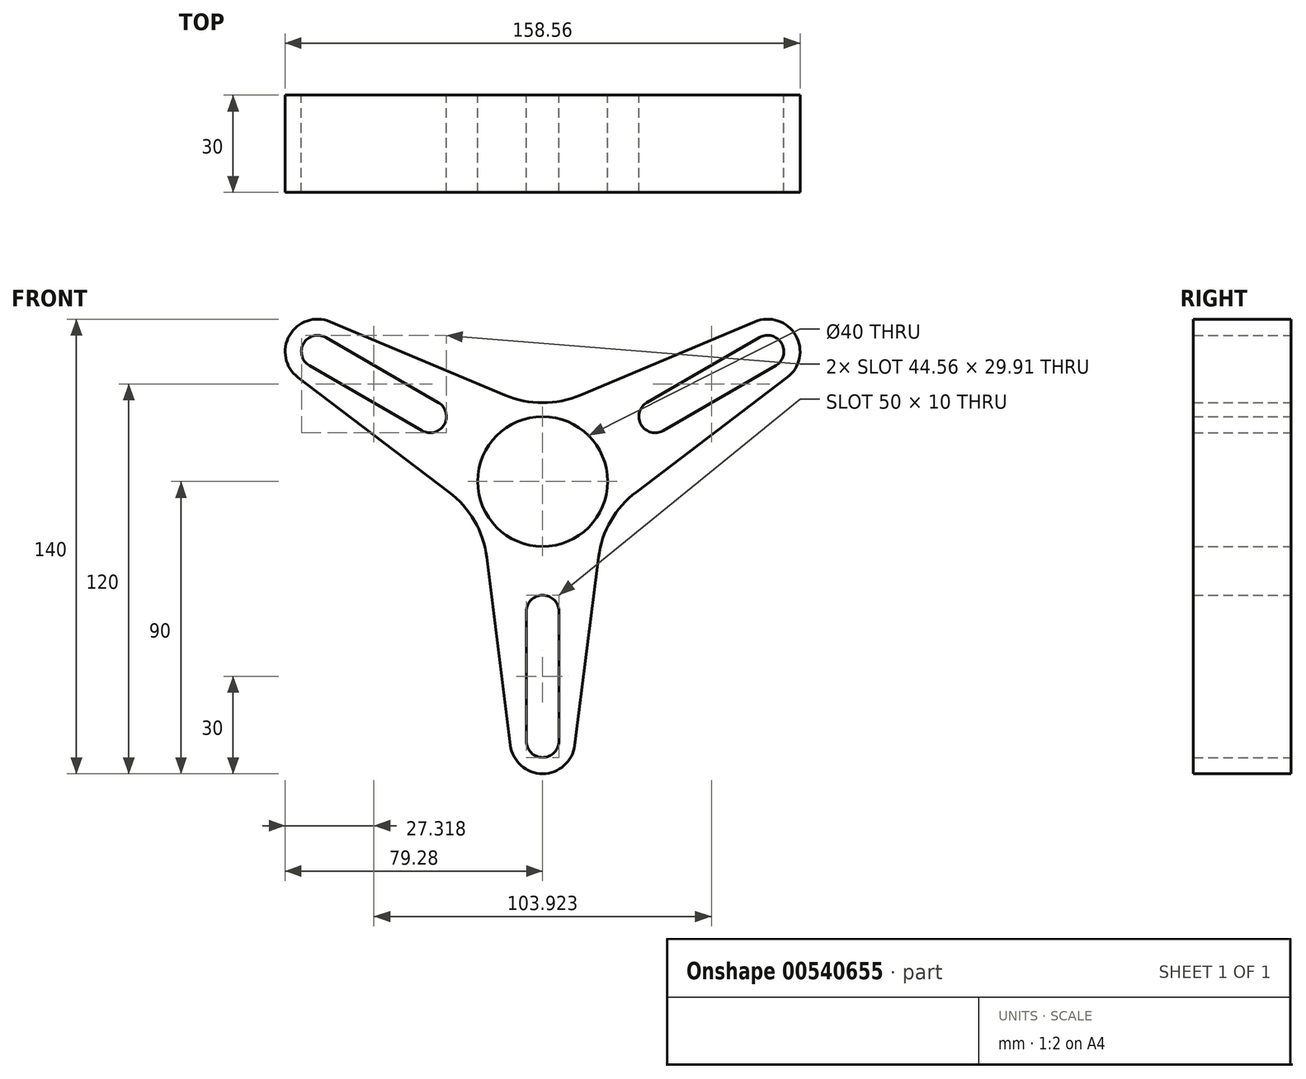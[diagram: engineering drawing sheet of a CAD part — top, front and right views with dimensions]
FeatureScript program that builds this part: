
annotation { "Feature Type Name" : "Feature", "Feature Type Description" : "" }
export const myFeature = defineFeature(function(context is Context, id is Id, definition is map)
    precondition{}
    {
        {
            var Q0;
            Q0=qCreatedBy(makeId("Front.planeOp"),FACE);
            var sketch = newSketch(context, id + "F0", { "sketchPlane" : qUnion([Q0])});
            skCircle(sketch, "E0", {"center": v(0, 0) * mm, "radius": 10 * mm});
            skCircle(sketch, "E1", {"center": v(0, 0) * mm, "radius": 20 * mm});
            skLineSegment(sketch, "E2", {"start": v(0, 0) * mm, "end": v(0, -90) * mm, "construction": true});
            skLineSegment(sketch, "E3", {"start": v(0, 0) * mm, "end": v(77.94, 45) * mm, "construction": true});
            skLineSegment(sketch, "E4", {"start": v(0, 0) * mm, "end": v(-77.94, 45) * mm, "construction": true});
            skPoint(sketch, "E5", {"position": v(0, -80) * mm});
            skPoint(sketch, "E6", {"position": v(-69.28, 40) * mm});
            skPoint(sketch, "E7", {"position": v(69.28, 40) * mm});
            skArc(sketch, "E8", {"start": v(-65.4, 49.22) * mm, "mid": v(-77.94, 45) * mm, "end": v(-75.33, 32.03) * mm});
            skArc(sketch, "E9", {"start": v(-66.78, 44.33) * mm, "mid": v(-73.61, 42.5) * mm, "end": v(-71.78, 35.67) * mm});
            skArc(sketch, "E10", {"start": v(75.33, 32.03) * mm, "mid": v(77.94, 45) * mm, "end": v(65.4, 49.22) * mm});
            skArc(sketch, "E11", {"start": v(71.78, 35.67) * mm, "mid": v(73.61, 42.5) * mm, "end": v(66.78, 44.33) * mm});
            skArc(sketch, "E12", {"start": v(-9.92, -81.25) * mm, "mid": v(0, -90) * mm, "end": v(9.92, -81.25) * mm});
            skArc(sketch, "E13", {"start": v(-5, -80) * mm, "mid": v(0, -85) * mm, "end": v(5, -80) * mm});
            skLineSegment(sketch, "E14", {"start": v(-9.92, -81.25) * mm, "end": v(-17.21, -23.37) * mm});
            skLineSegment(sketch, "E15", {"start": v(-28.85, -3.22) * mm, "end": v(-75.33, 32.03) * mm});
            skLineSegment(sketch, "E16", {"start": v(-65.4, 49.22) * mm, "end": v(-11.63, 26.6) * mm});
            skLineSegment(sketch, "E17", {"start": v(11.63, 26.6) * mm, "end": v(65.4, 49.22) * mm});
            skLineSegment(sketch, "E18", {"start": v(75.33, 32.03) * mm, "end": v(28.85, -3.22) * mm});
            skLineSegment(sketch, "E19", {"start": v(17.21, -23.37) * mm, "end": v(9.92, -81.25) * mm});
            skArc(sketch, "E20", {"start": v(-37.14, 15.67) * mm, "mid": v(-30.31, 17.5) * mm, "end": v(-32.14, 24.33) * mm});
            skArc(sketch, "E21", {"start": v(32.14, 24.33) * mm, "mid": v(30.31, 17.5) * mm, "end": v(37.14, 15.67) * mm});
            skArc(sketch, "E22", {"start": v(5, -40) * mm, "mid": v(0, -35) * mm, "end": v(-5, -40) * mm});
            skLineSegment(sketch, "E23", {"start": v(37.14, 15.67) * mm, "end": v(71.78, 35.67) * mm});
            skLineSegment(sketch, "E24", {"start": v(66.78, 44.33) * mm, "end": v(32.14, 24.33) * mm});
            skLineSegment(sketch, "E25", {"start": v(-37.14, 15.67) * mm, "end": v(-71.78, 35.67) * mm});
            skLineSegment(sketch, "E26", {"start": v(-66.78, 44.33) * mm, "end": v(-32.14, 24.33) * mm});
            skLineSegment(sketch, "E27", {"start": v(-5, -40) * mm, "end": v(-5, -80) * mm});
            skLineSegment(sketch, "E28", {"start": v(5, -40) * mm, "end": v(5, -80) * mm});
            skArc(sketch, "E29.filletArc", {"start": v(-17.21, -23.37) * mm, "mid": v(-21, -12.12) * mm, "end": v(-28.85, -3.22) * mm});
            skArc(sketch, "E30.filletArc", {"start": v(28.85, -3.22) * mm, "mid": v(21, -12.12) * mm, "end": v(17.21, -23.37) * mm});
            skArc(sketch, "E31.filletArc", {"start": v(-11.63, 26.6) * mm, "mid": v(0, 24.25) * mm, "end": v(11.63, 26.6) * mm});
            skSolve(sketch);
        }
        {
            var Q0;
            Q0 = qSketchRegion(id + "F0", true);
            extrude(context, id + "F1", {"entities" : qUnion([Q0]), "depth" : 30 * mm, "offsetDistance" : 25 * mm});
        }
    });
